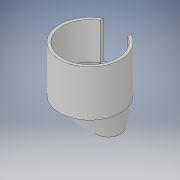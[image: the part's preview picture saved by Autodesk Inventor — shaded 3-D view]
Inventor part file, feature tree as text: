
AUTODESK INVENTOR PART (.ipt)
format: ipt  version: 2019 (Build 230136000, 136)  size: 240,640 bytes
history: native  units: mm
features: sketch x6, extrude x4, loft x2, fillet x2, other x2, plane x1
ambient origin geometry x8: Origin, YZ Plane, XZ Plane, XY Plane, X Axis, Y Axis, Z Axis, Center Point
bodies: Solid1 (feature_tree)
feature tree (17):
  extrude  "Extrusion1"  Depth=66.0mm
  extrude  "Extrusion2"  Depth=1.5mm
  extrude  "Extrusion3"  Depth=30.0mm
  sketch  "Sketch9"  dims[d7=60.0mm d8=10.0mm d9=0.0mm]
  plane  "Work Plane2"
  loft  "Loft1"
  extrude  "Extrusion6"  Depth=40.0mm
  loft  "Loft2"
  fillet  "Fillet1"  [1 undecoded]
  fillet  "Fillet2"  Radius=20.0mm
  sketch  "Sketch1"  dims[d0=60.0mm d1=66.0mm]
  sketch  "Sketch2"  dims[d2=40.0mm d3=0.0mm d4=1.5mm]
  sketch  "Sketch3"  dims[d5=1.5mm d6=30.0mm]
  sketch  "Sketch10"  dims[d10=10.0mm d11=0.0mm d21=40.0mm]
  sketch  "Sketch11"  dims[d22=26.0mm d23=0.0mm d24=90.0deg d25=0.0mm d26=90.0deg d27=20.0mm d28=20.0mm d29=0.0mm d30=0.0mm d31=90.0deg d32=0.0mm d33=90.0deg d34=10.0mm d35=10.0mm]
  other  "Edges1"
  other  "Edges2"
note: 1 required parameter value undecoded (feature->parameter linkage not recoverable at this tier; creation-order binding heuristic only, values carry confidence <= 0.55)
